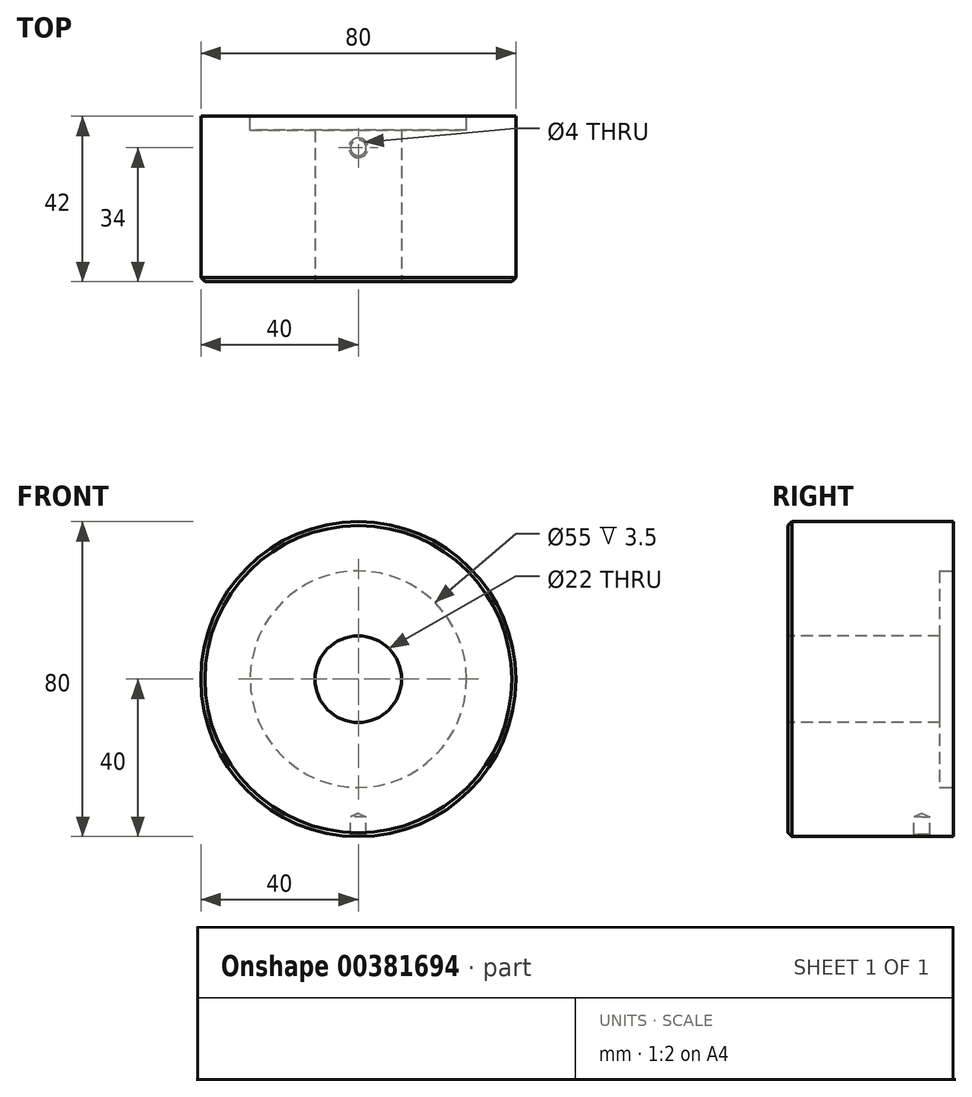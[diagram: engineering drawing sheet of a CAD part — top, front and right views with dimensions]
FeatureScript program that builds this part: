
annotation { "Feature Type Name" : "Feature", "Feature Type Description" : "" }
export const myFeature = defineFeature(function(context is Context, id is Id, definition is map)
    precondition{}
    {
        {
            var Q0;
            Q0=qCreatedBy(makeId("Front.planeOp"),FACE);
            var sketch = newSketch(context, id + "F0", { "sketchPlane" : qUnion([Q0])});
            skCircle(sketch, "E0", {"center": v(0, 0) * mm, "radius": 40 * mm});
            skSolve(sketch);
        }
        {
            var Q0;
            Q0 = qSketchRegion(id + "F0", true);
            extrude(context, id + "F1", {"entities" : qUnion([Q0]), "depth" : 42 * mm, "offsetDistance" : 25 * mm});
        }
        {
            var Q0;
            Q0=makeQuery(id+"F1.opExtrude","CAP_FACE",FACE,{"disambiguationData":[OSD([sQuery(id+"F0.wireOp",EDGE,"E0")])],"isStart":true});
            var sketch = newSketch(context, id + "F2", { "sketchPlane" : qUnion([Q0])});
            skCircle(sketch, "E1", {"center": v(0, 0) * mm, "radius": 27.5 * mm});
            skSolve(sketch);
        }
        {
            var Q0;
            Q0 = qSketchRegion(id + "F2", true);
            extrude(context, id + "F3", {"entities" : qUnion([Q0]), "operationType" : NewBodyOperationType.REMOVE, "oppositeDirection" : true, "depth" : 3.5 * mm, "offsetDistance" : 25 * mm});
        }
        {
            var Q0;
            Q0=makeQuery(id+"F1.opExtrude","CAP_FACE",FACE,{"disambiguationData":[OSD([sQuery(id+"F0.wireOp",EDGE,"E0")])],"isStart":false});
            var sketch = newSketch(context, id + "F4", { "sketchPlane" : qUnion([Q0])});
            skCircle(sketch, "E2", {"center": v(0, 0) * mm, "radius": 11 * mm});
            skSolve(sketch);
        }
        {
            var Q0;
            Q0 = qSketchRegion(id + "F4", true);
            extrude(context, id + "F5", {"entities" : qUnion([Q0]), "operationType" : NewBodyOperationType.REMOVE, "oppositeDirection" : true, "depth" : 105.4 * mm, "offsetDistance" : 25 * mm});
        }
        {
            var Q0;
            Q0=makeQuery(id+"F1.opExtrude","CAP_EDGE",EDGE,{"disambiguationData":[OSD([sQuery(id+"F0.wireOp",EDGE,"E0")])],"isStart":false});
            chamfer(context, id + "F6", {"entities" : qUnion([Q0]), "width" : 1 * mm, "tangentPropagation" : true});
        }
        {
            var Q0;
            Q0=qCreatedBy(makeId("Right.planeOp"),FACE);
            var sketch = newSketch(context, id + "F7", { "sketchPlane" : qUnion([Q0])});
            skLineSegment(sketch, "E3", {"start": v(-8, -46.2) * mm, "end": v(-8, -35) * mm});
            skLineSegment(sketch, "E4.0", {"start": v(-6, -39.5) * mm, "end": v(-6, -35) * mm});
            skLineSegment(sketch, "E5", {"start": v(-8, -46.2) * mm, "end": v(-6, -46.2) * mm});
            skPoint(sketch, "E6", {"position": v(-6, -39.5) * mm});
            skLineSegment(sketch, "E7", {"start": v(-6, -39.5) * mm, "end": v(-4.94, -40.56) * mm});
            skLineSegment(sketch, "E8", {"start": v(-6, -46.2) * mm, "end": v(-4.94, -40.56) * mm});
            skLineSegment(sketch, "E9", {"start": v(-6, -35) * mm, "end": v(-8, -34.1) * mm});
            skLineSegment(sketch, "E10", {"start": v(-8, -35) * mm, "end": v(-8, -34.1) * mm});
            skSolve(sketch);
        }
        {
            var Q0;
            Q0 = qSketchRegion(id + "F7", true);
            var Q1;
            Q1=sQuery(id+"F7.wireOp",EDGE,"E3");
            revolve(context, id + "F8", {"operationType" : NewBodyOperationType.REMOVE, "surfaceOperationType" : NewSurfaceOperationType.NEW, "entities" : qUnion([Q0]), "axis" : qUnion([Q1]), "revolveType" : RevolveType.FULL, "oppositeDirection" : true});
        }
    });
